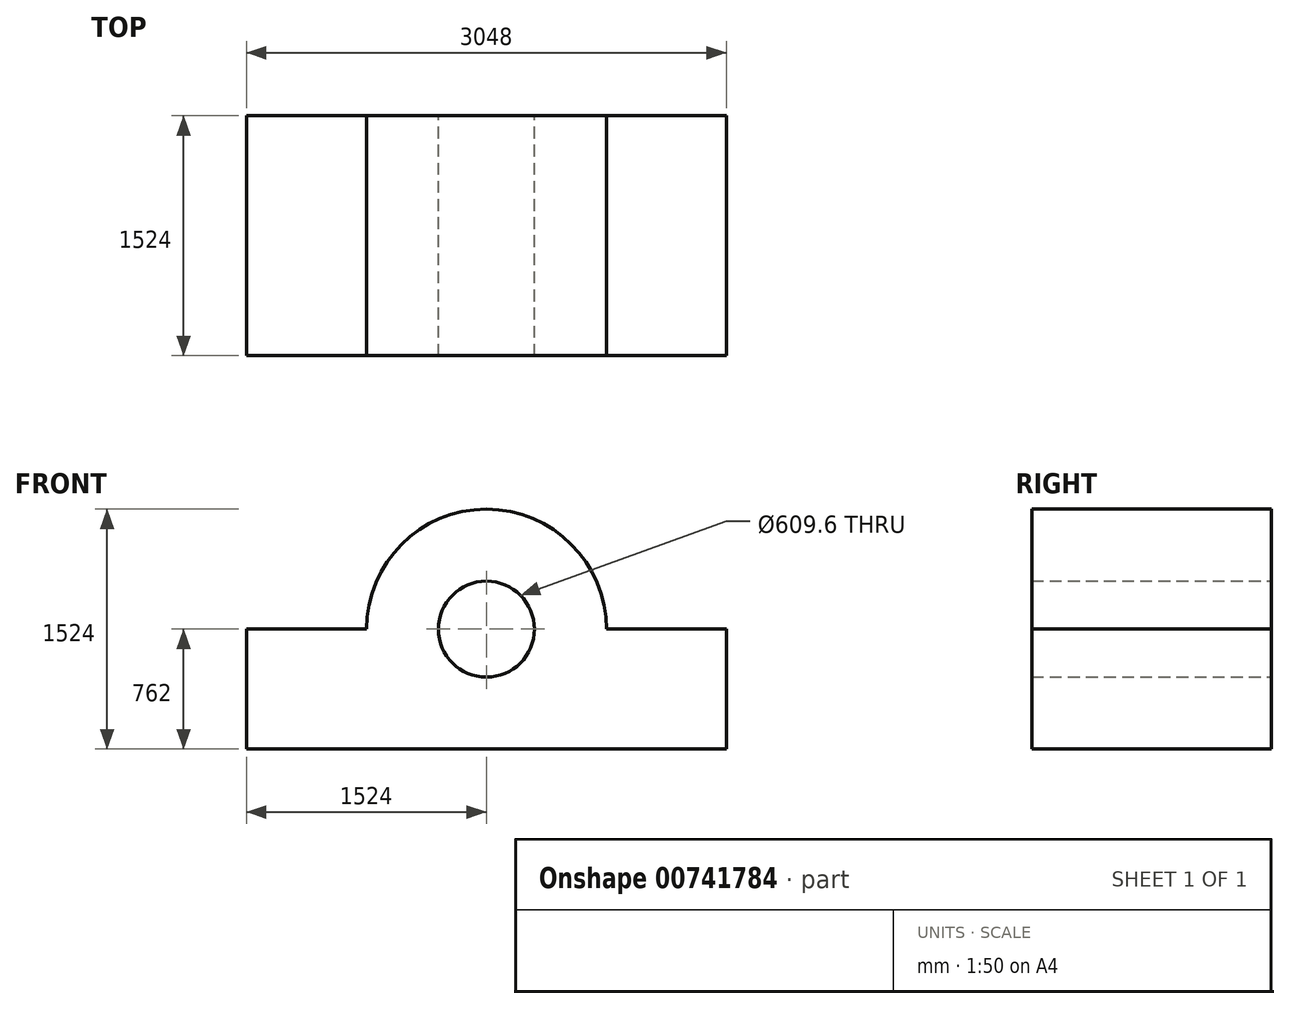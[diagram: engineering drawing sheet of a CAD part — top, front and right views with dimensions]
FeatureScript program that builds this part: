
annotation { "Feature Type Name" : "Feature", "Feature Type Description" : "" }
export const myFeature = defineFeature(function(context is Context, id is Id, definition is map)
    precondition{}
    {
        {
            var Q0;
            Q0=qCreatedBy(makeId("Front.planeOp"),FACE);
            var sketch = newSketch(context, id + "F0", { "sketchPlane" : qUnion([Q0])});
            skLineSegment(sketch, "E0", {"start": v(0, 0) * mm, "end": v(3048, 0) * mm});
            skLineSegment(sketch, "E1", {"start": v(3048, 0) * mm, "end": v(3048, 762) * mm});
            skLineSegment(sketch, "E2", {"start": v(0, 0) * mm, "end": v(0, 762) * mm});
            skLineSegment(sketch, "E3", {"start": v(0, 762) * mm, "end": v(762, 762) * mm});
            skLineSegment(sketch, "E4", {"start": v(3048, 762) * mm, "end": v(2286, 762) * mm});
            skArc(sketch, "E5", {"start": v(2286, 762) * mm, "mid": v(1524, 1524) * mm, "end": v(762, 762) * mm});
            skCircle(sketch, "E6", {"center": v(1524, 762) * mm, "radius": 304.8 * mm});
            skSolve(sketch);
        }
        {
            var Q0;
            Q0 = qSketchRegion(id + "F0", true);
            extrude(context, id + "F1", {"entities" : qUnion([Q0]), "depth" : 1524 * mm, "offsetDistance" : 25.4 * mm});
        }
    });
